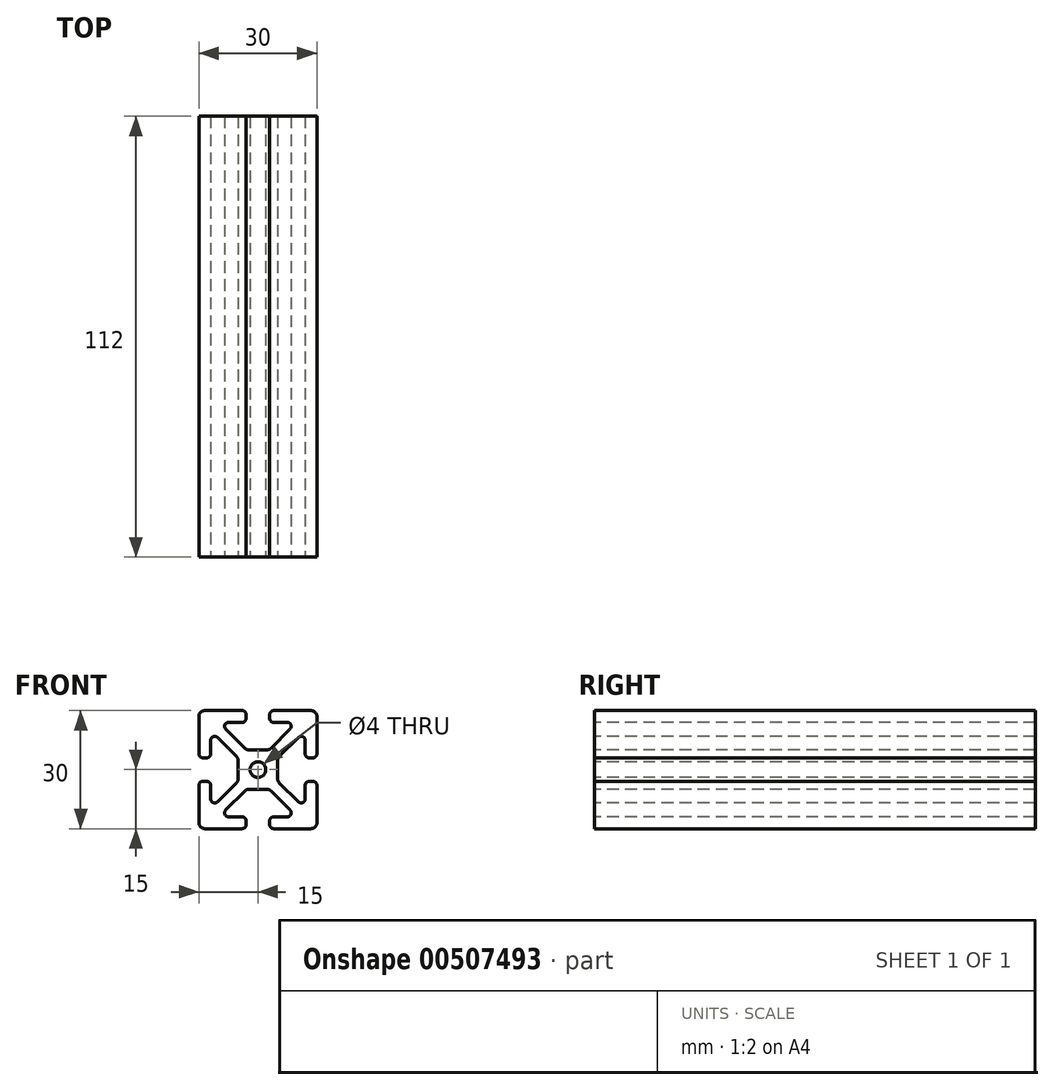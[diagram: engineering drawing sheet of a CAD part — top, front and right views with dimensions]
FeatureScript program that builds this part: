
annotation { "Feature Type Name" : "Feature", "Feature Type Description" : "" }
export const myFeature = defineFeature(function(context is Context, id is Id, definition is map)
    precondition{}
    {
        {
            var Q0;
            Q0=qCreatedBy(makeId("Front.planeOp"),FACE);
            var sketch = newSketch(context, id + "F0", { "sketchPlane" : qUnion([Q0])});
            skLineSegment(sketch, "E0.bottom", {"start": v(13.5, 15) * mm, "end": v(4, 15) * mm});
            skLineSegment(sketch, "E0.top", {"start": v(13.5, -15) * mm, "end": v(4, -15) * mm});
            skLineSegment(sketch, "E0.left", {"start": v(15, 13.5) * mm, "end": v(15, 4) * mm});
            skLineSegment(sketch, "E0.right", {"start": v(-15, 13.5) * mm, "end": v(-15, 4) * mm});
            skPoint(sketch, "E0.middle", {"position": v(0, 0) * mm});
            skLineSegment(sketch, "E1.bottom", {"start": v(7.46, 12) * mm, "end": v(4, 12) * mm});
            skLineSegment(sketch, "E1.top", {"start": v(7.46, -12) * mm, "end": v(4, -12) * mm});
            skLineSegment(sketch, "E1.left", {"start": v(12, 7.46) * mm, "end": v(12, 4) * mm});
            skLineSegment(sketch, "E1.right", {"start": v(-12, 7.46) * mm, "end": v(-12, 4) * mm});
            skLineSegment(sketch, "E2", {"start": v(8.17, 10.3) * mm, "end": v(3.32, 5.44) * mm});
            skLineSegment(sketch, "E3", {"start": v(-8.17, -10.3) * mm, "end": v(-3.32, -5.44) * mm});
            skLineSegment(sketch, "E4", {"start": v(-8.17, 10.3) * mm, "end": v(-3.32, 5.44) * mm});
            skLineSegment(sketch, "E5", {"start": v(-10.3, 8.17) * mm, "end": v(-5.44, 3.32) * mm});
            skPoint(sketch, "E6.orphan", {"position": v(12, 12) * mm});
            skPoint(sketch, "E7.orphan", {"position": v(12, -12) * mm});
            skPoint(sketch, "E8.orphan", {"position": v(-12, -12) * mm});
            skPoint(sketch, "E9.orphan", {"position": v(-12, 12) * mm});
            skLineSegment(sketch, "E10.trimOffspring", {"start": v(-5.44, -3.32) * mm, "end": v(-10.3, -8.17) * mm});
            skLineSegment(sketch, "E11.trimOffspring", {"start": v(5.44, -3.32) * mm, "end": v(10.3, -8.17) * mm});
            skLineSegment(sketch, "E12.trimOffspring", {"start": v(5.44, 3.32) * mm, "end": v(10.3, 8.17) * mm});
            skLineSegment(sketch, "E13.trimOffspring", {"start": v(3.32, -5.44) * mm, "end": v(8.17, -10.3) * mm});
            skLineSegment(sketch, "E14.bottom", {"start": v(2.26, 5) * mm, "end": v(-2.26, 5) * mm});
            skLineSegment(sketch, "E14.top", {"start": v(2.26, -5) * mm, "end": v(-2.26, -5) * mm});
            skLineSegment(sketch, "E14.left", {"start": v(5, 2.26) * mm, "end": v(5, -2.26) * mm});
            skLineSegment(sketch, "E14.right", {"start": v(-5, 2.26) * mm, "end": v(-5, -2.26) * mm});
            skPoint(sketch, "E15.orphan", {"position": v(5, 5) * mm});
            skPoint(sketch, "E16.orphan", {"position": v(5, -5) * mm});
            skPoint(sketch, "E17.orphan", {"position": v(-5, -5) * mm});
            skPoint(sketch, "E18.orphan", {"position": v(-5, 5) * mm});
            skCircle(sketch, "E19", {"center": v(0, 0) * mm, "radius": 2 * mm});
            skLineSegment(sketch, "E20", {"start": v(-3, 14) * mm, "end": v(-3, 13) * mm});
            skLineSegment(sketch, "E21", {"start": v(3, 14) * mm, "end": v(3, 13) * mm});
            skLineSegment(sketch, "E22.trimOffspring", {"start": v(-3, -13) * mm, "end": v(-3, -14) * mm});
            skLineSegment(sketch, "E23.trimOffspring", {"start": v(-4, 12) * mm, "end": v(-7.46, 12) * mm});
            skLineSegment(sketch, "E24.trimOffspring", {"start": v(-4, 15) * mm, "end": v(-13.5, 15) * mm});
            skLineSegment(sketch, "E25.trimOffspring", {"start": v(3, -13) * mm, "end": v(3, -14) * mm});
            skLineSegment(sketch, "E26.trimOffspring", {"start": v(-4, -12) * mm, "end": v(-7.46, -12) * mm});
            skLineSegment(sketch, "E27.trimOffspring", {"start": v(-4, -15) * mm, "end": v(-13.5, -15) * mm});
            skLineSegment(sketch, "E28", {"start": v(-14, 3) * mm, "end": v(-13, 3) * mm});
            skLineSegment(sketch, "E29", {"start": v(-14, -3) * mm, "end": v(-13, -3) * mm});
            skLineSegment(sketch, "E30.trimOffspring", {"start": v(-12, -4) * mm, "end": v(-12, -7.46) * mm});
            skLineSegment(sketch, "E31.trimOffspring", {"start": v(-15, -4) * mm, "end": v(-15, -13.5) * mm});
            skLineSegment(sketch, "E32.trimOffspring", {"start": v(13, 3) * mm, "end": v(14, 3) * mm});
            skLineSegment(sketch, "E33.trimOffspring", {"start": v(13, -3) * mm, "end": v(14, -3) * mm});
            skLineSegment(sketch, "E34.trimOffspring", {"start": v(12, -4) * mm, "end": v(12, -7.46) * mm});
            skLineSegment(sketch, "E35.trimOffspring", {"start": v(15, -4) * mm, "end": v(15, -13.5) * mm});
            skPoint(sketch, "E36.visualSharp", {"position": v(-15, 15) * mm});
            skArc(sketch, "E36.filletArc", {"start": v(-13.5, 15) * mm, "mid": v(-14.56, 14.56) * mm, "end": v(-15, 13.5) * mm});
            skPoint(sketch, "E37.visualSharp", {"position": v(15, 15) * mm});
            skArc(sketch, "E37.filletArc", {"start": v(15, 13.5) * mm, "mid": v(14.56, 14.56) * mm, "end": v(13.5, 15) * mm});
            skPoint(sketch, "E38.visualSharp", {"position": v(15, -15) * mm});
            skArc(sketch, "E38.filletArc", {"start": v(13.5, -15) * mm, "mid": v(14.56, -14.56) * mm, "end": v(15, -13.5) * mm});
            skPoint(sketch, "E39.visualSharp", {"position": v(-15, -15) * mm});
            skArc(sketch, "E39.filletArc", {"start": v(-15, -13.5) * mm, "mid": v(-14.56, -14.56) * mm, "end": v(-13.5, -15) * mm});
            skPoint(sketch, "E40.visualSharp", {"position": v(-5, -2.88) * mm});
            skArc(sketch, "E40.filletArc", {"start": v(-5.44, -3.32) * mm, "mid": v(-5.11, -2.83) * mm, "end": v(-5, -2.26) * mm});
            skPoint(sketch, "E41.visualSharp", {"position": v(-2.88, -5) * mm});
            skArc(sketch, "E41.filletArc", {"start": v(-2.26, -5) * mm, "mid": v(-2.83, -5.11) * mm, "end": v(-3.32, -5.44) * mm});
            skPoint(sketch, "E42.visualSharp", {"position": v(2.88, -5) * mm});
            skArc(sketch, "E42.filletArc", {"start": v(3.32, -5.44) * mm, "mid": v(2.83, -5.11) * mm, "end": v(2.26, -5) * mm});
            skPoint(sketch, "E43.visualSharp", {"position": v(5, -2.88) * mm});
            skArc(sketch, "E43.filletArc", {"start": v(5, -2.26) * mm, "mid": v(5.11, -2.83) * mm, "end": v(5.44, -3.32) * mm});
            skPoint(sketch, "E44.visualSharp", {"position": v(5, 2.88) * mm});
            skArc(sketch, "E44.filletArc", {"start": v(5.44, 3.32) * mm, "mid": v(5.11, 2.83) * mm, "end": v(5, 2.26) * mm});
            skPoint(sketch, "E45.visualSharp", {"position": v(2.88, 5) * mm});
            skArc(sketch, "E45.filletArc", {"start": v(2.26, 5) * mm, "mid": v(2.83, 5.11) * mm, "end": v(3.32, 5.44) * mm});
            skPoint(sketch, "E46.visualSharp", {"position": v(-2.88, 5) * mm});
            skArc(sketch, "E46.filletArc", {"start": v(-3.32, 5.44) * mm, "mid": v(-2.83, 5.11) * mm, "end": v(-2.26, 5) * mm});
            skPoint(sketch, "E47.visualSharp", {"position": v(-3, 12) * mm});
            skArc(sketch, "E47.filletArc", {"start": v(-4, 12) * mm, "mid": v(-3.3, 12.3) * mm, "end": v(-3, 13) * mm});
            skPoint(sketch, "E48.visualSharp", {"position": v(-3, 15) * mm});
            skArc(sketch, "E48.filletArc", {"start": v(-3, 14) * mm, "mid": v(-3.3, 14.7) * mm, "end": v(-4, 15) * mm});
            skPoint(sketch, "E49.visualSharp", {"position": v(3, 15) * mm});
            skArc(sketch, "E49.filletArc", {"start": v(4, 15) * mm, "mid": v(3.3, 14.7) * mm, "end": v(3, 14) * mm});
            skPoint(sketch, "E50.visualSharp", {"position": v(3, 12) * mm});
            skArc(sketch, "E50.filletArc", {"start": v(3, 13) * mm, "mid": v(3.3, 12.3) * mm, "end": v(4, 12) * mm});
            skPoint(sketch, "E51.visualSharp", {"position": v(12, 3) * mm});
            skArc(sketch, "E51.filletArc", {"start": v(12, 4) * mm, "mid": v(12.3, 3.3) * mm, "end": v(13, 3) * mm});
            skPoint(sketch, "E52.visualSharp", {"position": v(15, 3) * mm});
            skArc(sketch, "E52.filletArc", {"start": v(14, 3) * mm, "mid": v(14.7, 3.3) * mm, "end": v(15, 4) * mm});
            skPoint(sketch, "E53.visualSharp", {"position": v(15, -3) * mm});
            skArc(sketch, "E53.filletArc", {"start": v(15, -4) * mm, "mid": v(14.7, -3.3) * mm, "end": v(14, -3) * mm});
            skPoint(sketch, "E54.visualSharp", {"position": v(12, -3) * mm});
            skArc(sketch, "E54.filletArc", {"start": v(13, -3) * mm, "mid": v(12.3, -3.3) * mm, "end": v(12, -4) * mm});
            skPoint(sketch, "E55.visualSharp", {"position": v(3, -12) * mm});
            skArc(sketch, "E55.filletArc", {"start": v(4, -12) * mm, "mid": v(3.3, -12.3) * mm, "end": v(3, -13) * mm});
            skPoint(sketch, "E56.visualSharp", {"position": v(3, -15) * mm});
            skArc(sketch, "E56.filletArc", {"start": v(3, -14) * mm, "mid": v(3.3, -14.7) * mm, "end": v(4, -15) * mm});
            skPoint(sketch, "E57.visualSharp", {"position": v(-3, -12) * mm});
            skArc(sketch, "E57.filletArc", {"start": v(-3, -13) * mm, "mid": v(-3.3, -12.3) * mm, "end": v(-4, -12) * mm});
            skPoint(sketch, "E58.visualSharp", {"position": v(-3, -15) * mm});
            skArc(sketch, "E58.filletArc", {"start": v(-4, -15) * mm, "mid": v(-3.3, -14.7) * mm, "end": v(-3, -14) * mm});
            skPoint(sketch, "E59.visualSharp", {"position": v(-12, -3) * mm});
            skArc(sketch, "E59.filletArc", {"start": v(-12, -4) * mm, "mid": v(-12.3, -3.3) * mm, "end": v(-13, -3) * mm});
            skPoint(sketch, "E60.visualSharp", {"position": v(-15, -3) * mm});
            skArc(sketch, "E60.filletArc", {"start": v(-14, -3) * mm, "mid": v(-14.7, -3.3) * mm, "end": v(-15, -4) * mm});
            skPoint(sketch, "E61.visualSharp", {"position": v(-15, 3) * mm});
            skArc(sketch, "E61.filletArc", {"start": v(-15, 4) * mm, "mid": v(-14.7, 3.3) * mm, "end": v(-14, 3) * mm});
            skPoint(sketch, "E62.visualSharp", {"position": v(-12, 3) * mm});
            skArc(sketch, "E62.filletArc", {"start": v(-13, 3) * mm, "mid": v(-12.3, 3.3) * mm, "end": v(-12, 4) * mm});
            skPoint(sketch, "E63.visualSharp", {"position": v(9.88, 12) * mm});
            skArc(sketch, "E63.filletArc", {"start": v(8.17, 10.3) * mm, "mid": v(8.39, 11.38) * mm, "end": v(7.46, 12) * mm});
            skPoint(sketch, "E64.visualSharp", {"position": v(12, 9.88) * mm});
            skArc(sketch, "E64.filletArc", {"start": v(12, 7.46) * mm, "mid": v(11.38, 8.39) * mm, "end": v(10.3, 8.17) * mm});
            skPoint(sketch, "E65.visualSharp", {"position": v(12, -9.88) * mm});
            skArc(sketch, "E65.filletArc", {"start": v(10.3, -8.17) * mm, "mid": v(11.38, -8.39) * mm, "end": v(12, -7.46) * mm});
            skPoint(sketch, "E66.visualSharp", {"position": v(9.88, -12) * mm});
            skArc(sketch, "E66.filletArc", {"start": v(7.46, -12) * mm, "mid": v(8.39, -11.38) * mm, "end": v(8.17, -10.3) * mm});
            skPoint(sketch, "E67.visualSharp", {"position": v(-12, -9.88) * mm});
            skArc(sketch, "E67.filletArc", {"start": v(-12, -7.46) * mm, "mid": v(-11.38, -8.39) * mm, "end": v(-10.3, -8.17) * mm});
            skPoint(sketch, "E68.visualSharp", {"position": v(-9.88, -12) * mm});
            skArc(sketch, "E68.filletArc", {"start": v(-8.17, -10.3) * mm, "mid": v(-8.39, -11.38) * mm, "end": v(-7.46, -12) * mm});
            skPoint(sketch, "E69.visualSharp", {"position": v(-12, 9.88) * mm});
            skArc(sketch, "E69.filletArc", {"start": v(-10.3, 8.17) * mm, "mid": v(-11.38, 8.39) * mm, "end": v(-12, 7.46) * mm});
            skPoint(sketch, "E70.visualSharp", {"position": v(-9.88, 12) * mm});
            skArc(sketch, "E70.filletArc", {"start": v(-7.46, 12) * mm, "mid": v(-8.39, 11.38) * mm, "end": v(-8.17, 10.3) * mm});
            skPoint(sketch, "E71.visualSharp", {"position": v(-5, 2.88) * mm});
            skArc(sketch, "E71.filletArc", {"start": v(-5, 2.26) * mm, "mid": v(-5.11, 2.83) * mm, "end": v(-5.44, 3.32) * mm});
            skSolve(sketch);
        }
        {
            var Q0;
            Q0=qSketchRegion(id+"F0",true);
            extrude(context, id + "F1", {"entities" : qUnion([Q0]), "oppositeDirection" : true, "depth" : 112 * mm});
        }
    });
